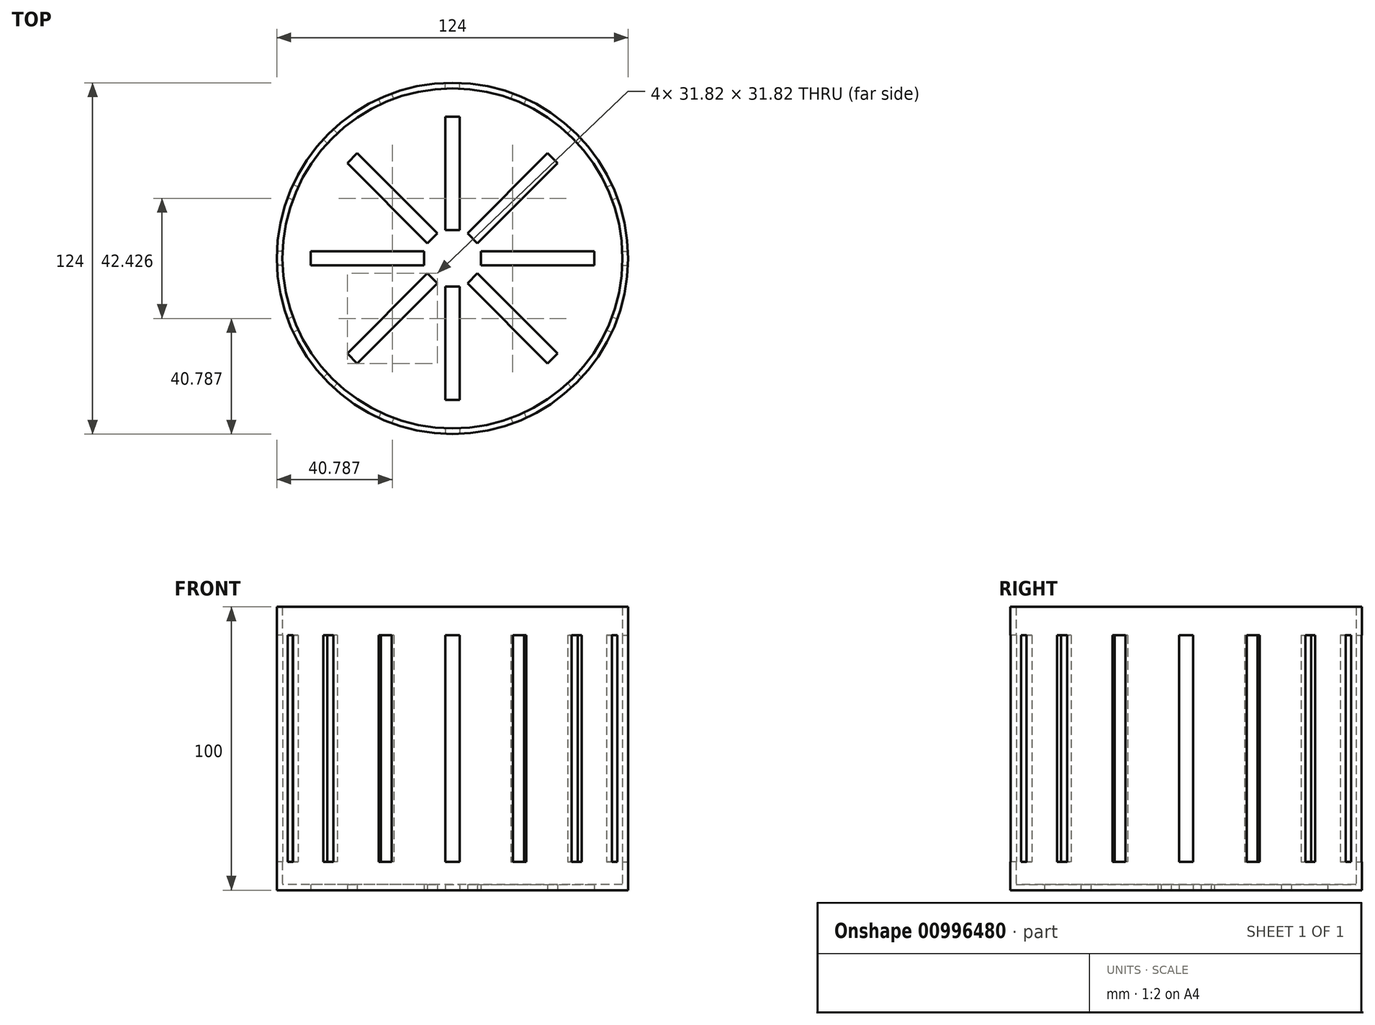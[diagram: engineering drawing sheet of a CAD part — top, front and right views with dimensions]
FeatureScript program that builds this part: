
annotation { "Feature Type Name" : "Feature", "Feature Type Description" : "" }
export const myFeature = defineFeature(function(context is Context, id is Id, definition is map)
    precondition{}
    {
        {
            var Q0;
            Q0=qCreatedBy(makeId("Top.planeOp"),FACE);
            var sketch = newSketch(context, id + "F0", { "sketchPlane" : qUnion([Q0])});
            skCircle(sketch, "E0", {"center": v(0, 0) * mm, "radius": 60 * mm});
            skLineSegment(sketch, "E1", {"start": v(0, 66.92) * mm, "end": v(0, -68.72) * mm, "construction": true});
            skLineSegment(sketch, "E2.bottom", {"start": v(2.5, 10) * mm, "end": v(-2.5, 10) * mm});
            skLineSegment(sketch, "E2.top", {"start": v(2.5, 50) * mm, "end": v(-2.5, 50) * mm});
            skLineSegment(sketch, "E2.left", {"start": v(2.5, 10) * mm, "end": v(2.5, 50) * mm});
            skLineSegment(sketch, "E2.right", {"start": v(-2.5, 10) * mm, "end": v(-2.5, 50) * mm});
            skPoint(sketch, "E2.middle", {"position": v(0, 30) * mm});
            skPoint(sketch, "E3.1.0", {"position": v(-21.21, 21.21) * mm});
            skLineSegment(sketch, "E3.1.1", {"start": v(-8.84, 5.3) * mm, "end": v(-37.12, 33.59) * mm});
            skLineSegment(sketch, "E3.1.2", {"start": v(-5.3, 8.84) * mm, "end": v(-33.59, 37.12) * mm});
            skLineSegment(sketch, "E3.1.3", {"start": v(-33.59, 37.12) * mm, "end": v(-37.12, 33.59) * mm});
            skLineSegment(sketch, "E3.1.4", {"start": v(-5.3, 8.84) * mm, "end": v(-8.84, 5.3) * mm});
            skPoint(sketch, "E3.2.0", {"position": v(-30, 0) * mm});
            skLineSegment(sketch, "E3.2.1", {"start": v(-10, -2.5) * mm, "end": v(-50, -2.5) * mm});
            skLineSegment(sketch, "E3.2.2", {"start": v(-10, 2.5) * mm, "end": v(-50, 2.5) * mm});
            skLineSegment(sketch, "E3.2.3", {"start": v(-50, 2.5) * mm, "end": v(-50, -2.5) * mm});
            skLineSegment(sketch, "E3.2.4", {"start": v(-10, 2.5) * mm, "end": v(-10, -2.5) * mm});
            skPoint(sketch, "E3.3.0", {"position": v(-21.21, -21.21) * mm});
            skLineSegment(sketch, "E3.3.1", {"start": v(-5.3, -8.84) * mm, "end": v(-33.59, -37.12) * mm});
            skLineSegment(sketch, "E3.3.2", {"start": v(-8.84, -5.3) * mm, "end": v(-37.12, -33.59) * mm});
            skLineSegment(sketch, "E3.3.3", {"start": v(-37.12, -33.59) * mm, "end": v(-33.59, -37.12) * mm});
            skLineSegment(sketch, "E3.3.4", {"start": v(-8.84, -5.3) * mm, "end": v(-5.3, -8.84) * mm});
            skPoint(sketch, "E3.4.0", {"position": v(0, -30) * mm});
            skLineSegment(sketch, "E3.4.1", {"start": v(2.5, -10) * mm, "end": v(2.5, -50) * mm});
            skLineSegment(sketch, "E3.4.2", {"start": v(-2.5, -10) * mm, "end": v(-2.5, -50) * mm});
            skLineSegment(sketch, "E3.4.3", {"start": v(-2.5, -50) * mm, "end": v(2.5, -50) * mm});
            skLineSegment(sketch, "E3.4.4", {"start": v(-2.5, -10) * mm, "end": v(2.5, -10) * mm});
            skPoint(sketch, "E3.5.0", {"position": v(21.21, -21.21) * mm});
            skLineSegment(sketch, "E3.5.1", {"start": v(8.84, -5.3) * mm, "end": v(37.12, -33.59) * mm});
            skLineSegment(sketch, "E3.5.2", {"start": v(5.3, -8.84) * mm, "end": v(33.59, -37.12) * mm});
            skLineSegment(sketch, "E3.5.3", {"start": v(33.59, -37.12) * mm, "end": v(37.12, -33.59) * mm});
            skLineSegment(sketch, "E3.5.4", {"start": v(5.3, -8.84) * mm, "end": v(8.84, -5.3) * mm});
            skPoint(sketch, "E3.6.0", {"position": v(30, 0) * mm});
            skLineSegment(sketch, "E3.6.1", {"start": v(10, 2.5) * mm, "end": v(50, 2.5) * mm});
            skLineSegment(sketch, "E3.6.2", {"start": v(10, -2.5) * mm, "end": v(50, -2.5) * mm});
            skLineSegment(sketch, "E3.6.3", {"start": v(50, -2.5) * mm, "end": v(50, 2.5) * mm});
            skLineSegment(sketch, "E3.6.4", {"start": v(10, -2.5) * mm, "end": v(10, 2.5) * mm});
            skPoint(sketch, "E3.7.0", {"position": v(21.21, 21.21) * mm});
            skLineSegment(sketch, "E3.7.1", {"start": v(5.3, 8.84) * mm, "end": v(33.59, 37.12) * mm});
            skLineSegment(sketch, "E3.7.2", {"start": v(8.84, 5.3) * mm, "end": v(37.12, 33.59) * mm});
            skLineSegment(sketch, "E3.7.3", {"start": v(37.12, 33.59) * mm, "end": v(33.59, 37.12) * mm});
            skLineSegment(sketch, "E3.7.4", {"start": v(8.84, 5.3) * mm, "end": v(5.3, 8.84) * mm});
            skCircle(sketch, "E4", {"center": v(0, 0) * mm, "radius": 62 * mm});
            skLineSegment(sketch, "E5", {"start": v(-2.5, -59.95) * mm, "end": v(-2.5, -61.95) * mm});
            skLineSegment(sketch, "E6", {"start": v(2.5, -59.95) * mm, "end": v(2.5, -61.95) * mm});
            skSolve(sketch);
        }
        {
            var Q0;
            Q0=makeQuery(id+"F0.imprint","IMPRINT",FACE,{"disambiguationData":[TD([[makeQuery(id+"F0.imprint","IMPRINT",EDGE,{"derivedFrom":sQuery(id+"F0.wireOp",EDGE,"E0")}),1.0]])]});
            var Q1;
            Q1=makeQuery(id+"F0.imprint","IMPRINT",FACE,{"disambiguationData":[TD([[makeQuery(id+"F0.imprint","IMPRINT",EDGE,{"derivedFrom":sQuery(id+"F0.wireOp",EDGE,"E0")}),-1.0]])]});
            extrude(context, id + "F1", {"entities" : qUnion([Q0, Q1]), "depth" : 2 * mm, "offsetDistance" : 25 * mm});
        }
        {
            var Q0;
            Q0=makeQuery(id+"F0.imprint","IMPRINT",FACE,{"disambiguationData":[TD([[makeQuery(id+"F0.imprint","IMPRINT",EDGE,{"derivedFrom":sQuery(id+"F0.wireOp",EDGE,"E0")}),-1.0]])]});
            extrude(context, id + "F2", {"entities" : qUnion([Q0]), "operationType" : NewBodyOperationType.ADD, "depth" : 100 * mm, "offsetDistance" : 25 * mm});
        }
        {
            var Q0;
            Q0=qCreatedBy(makeId("Top.planeOp"),FACE);
            cPlane(context, id + "F3", {"entities" : qUnion([Q0]), "cplaneType" : CPlaneType.OFFSET, "offset" : 10 * mm, "width" : 150 * mm, "height" : 150 * mm});
        }
        {
            var Q0;
            Q0=qCreatedBy(id+"F3.planeOp",FACE);
            var sketch = newSketch(context, id + "F4", { "sketchPlane" : qUnion([Q0])});
            skLineSegment(sketch, "E7", {"start": v(-2.5, -59.95) * mm, "end": v(-2.5, -61.95) * mm});
            skLineSegment(sketch, "E8", {"start": v(2.5, -59.95) * mm, "end": v(2.5, -61.95) * mm});
            skArc(sketch, "E9", {"start": v(-2.5, -61.95) * mm, "mid": v(0, -62.08) * mm, "end": v(2.5, -61.95) * mm});
            skArc(sketch, "E10", {"start": v(-2.5, -59.95) * mm, "mid": v(0, -59.8) * mm, "end": v(2.5, -59.95) * mm});
            skArc(sketch, "E11.1.0", {"start": v(21.4, -58.2) * mm, "mid": v(23.76, -57.35) * mm, "end": v(26.02, -56.28) * mm});
            skArc(sketch, "E11.1.1", {"start": v(20.63, -56.34) * mm, "mid": v(22.89, -55.25) * mm, "end": v(25.25, -54.43) * mm});
            skLineSegment(sketch, "E11.1.2", {"start": v(20.63, -56.34) * mm, "end": v(21.4, -58.2) * mm});
            skLineSegment(sketch, "E11.1.3", {"start": v(25.25, -54.43) * mm, "end": v(26.02, -56.28) * mm});
            skArc(sketch, "E11.2.0", {"start": v(42.04, -45.57) * mm, "mid": v(43.9, -43.9) * mm, "end": v(45.57, -42.04) * mm});
            skArc(sketch, "E11.2.1", {"start": v(40.62, -44.16) * mm, "mid": v(42.29, -42.29) * mm, "end": v(44.16, -40.62) * mm});
            skLineSegment(sketch, "E11.2.2", {"start": v(40.62, -44.16) * mm, "end": v(42.04, -45.57) * mm});
            skLineSegment(sketch, "E11.2.3", {"start": v(44.16, -40.62) * mm, "end": v(45.57, -42.04) * mm});
            skArc(sketch, "E11.3.0", {"start": v(56.28, -26.02) * mm, "mid": v(57.35, -23.76) * mm, "end": v(58.2, -21.4) * mm});
            skArc(sketch, "E11.3.1", {"start": v(54.43, -25.25) * mm, "mid": v(55.25, -22.89) * mm, "end": v(56.34, -20.63) * mm});
            skLineSegment(sketch, "E11.3.2", {"start": v(54.43, -25.25) * mm, "end": v(56.28, -26.02) * mm});
            skLineSegment(sketch, "E11.3.3", {"start": v(56.34, -20.63) * mm, "end": v(58.2, -21.4) * mm});
            skArc(sketch, "E11.4.0", {"start": v(61.95, -2.5) * mm, "mid": v(62.08, 0) * mm, "end": v(61.95, 2.5) * mm});
            skArc(sketch, "E11.4.1", {"start": v(59.95, -2.5) * mm, "mid": v(59.8, 0) * mm, "end": v(59.95, 2.5) * mm});
            skLineSegment(sketch, "E11.4.2", {"start": v(59.95, -2.5) * mm, "end": v(61.95, -2.5) * mm});
            skLineSegment(sketch, "E11.4.3", {"start": v(59.95, 2.5) * mm, "end": v(61.95, 2.5) * mm});
            skArc(sketch, "E11.5.0", {"start": v(58.2, 21.4) * mm, "mid": v(57.35, 23.76) * mm, "end": v(56.28, 26.02) * mm});
            skArc(sketch, "E11.5.1", {"start": v(56.34, 20.63) * mm, "mid": v(55.25, 22.89) * mm, "end": v(54.43, 25.25) * mm});
            skLineSegment(sketch, "E11.5.2", {"start": v(56.34, 20.63) * mm, "end": v(58.2, 21.4) * mm});
            skLineSegment(sketch, "E11.5.3", {"start": v(54.43, 25.25) * mm, "end": v(56.28, 26.02) * mm});
            skArc(sketch, "E11.6.0", {"start": v(45.57, 42.04) * mm, "mid": v(43.9, 43.9) * mm, "end": v(42.04, 45.57) * mm});
            skArc(sketch, "E11.6.1", {"start": v(44.16, 40.62) * mm, "mid": v(42.29, 42.29) * mm, "end": v(40.62, 44.16) * mm});
            skLineSegment(sketch, "E11.6.2", {"start": v(44.16, 40.62) * mm, "end": v(45.57, 42.04) * mm});
            skLineSegment(sketch, "E11.6.3", {"start": v(40.62, 44.16) * mm, "end": v(42.04, 45.57) * mm});
            skArc(sketch, "E11.7.0", {"start": v(26.02, 56.28) * mm, "mid": v(23.76, 57.35) * mm, "end": v(21.4, 58.2) * mm});
            skArc(sketch, "E11.7.1", {"start": v(25.25, 54.43) * mm, "mid": v(22.89, 55.25) * mm, "end": v(20.63, 56.34) * mm});
            skLineSegment(sketch, "E11.7.2", {"start": v(25.25, 54.43) * mm, "end": v(26.02, 56.28) * mm});
            skLineSegment(sketch, "E11.7.3", {"start": v(20.63, 56.34) * mm, "end": v(21.4, 58.2) * mm});
            skArc(sketch, "E11.8.0", {"start": v(2.5, 61.95) * mm, "mid": v(0, 62.08) * mm, "end": v(-2.5, 61.95) * mm});
            skArc(sketch, "E11.8.1", {"start": v(2.5, 59.95) * mm, "mid": v(0, 59.8) * mm, "end": v(-2.5, 59.95) * mm});
            skLineSegment(sketch, "E11.8.2", {"start": v(2.5, 59.95) * mm, "end": v(2.5, 61.95) * mm});
            skLineSegment(sketch, "E11.8.3", {"start": v(-2.5, 59.95) * mm, "end": v(-2.5, 61.95) * mm});
            skArc(sketch, "E11.9.0", {"start": v(-21.4, 58.2) * mm, "mid": v(-23.76, 57.35) * mm, "end": v(-26.02, 56.28) * mm});
            skArc(sketch, "E11.9.1", {"start": v(-20.63, 56.34) * mm, "mid": v(-22.89, 55.25) * mm, "end": v(-25.25, 54.43) * mm});
            skLineSegment(sketch, "E11.9.2", {"start": v(-20.63, 56.34) * mm, "end": v(-21.4, 58.2) * mm});
            skLineSegment(sketch, "E11.9.3", {"start": v(-25.25, 54.43) * mm, "end": v(-26.02, 56.28) * mm});
            skArc(sketch, "E11.10.0", {"start": v(-42.04, 45.57) * mm, "mid": v(-43.9, 43.9) * mm, "end": v(-45.57, 42.04) * mm});
            skArc(sketch, "E11.10.1", {"start": v(-40.62, 44.16) * mm, "mid": v(-42.29, 42.29) * mm, "end": v(-44.16, 40.62) * mm});
            skLineSegment(sketch, "E11.10.2", {"start": v(-40.62, 44.16) * mm, "end": v(-42.04, 45.57) * mm});
            skLineSegment(sketch, "E11.10.3", {"start": v(-44.16, 40.62) * mm, "end": v(-45.57, 42.04) * mm});
            skArc(sketch, "E11.11.0", {"start": v(-56.28, 26.02) * mm, "mid": v(-57.35, 23.76) * mm, "end": v(-58.2, 21.4) * mm});
            skArc(sketch, "E11.11.1", {"start": v(-54.43, 25.25) * mm, "mid": v(-55.25, 22.89) * mm, "end": v(-56.34, 20.63) * mm});
            skLineSegment(sketch, "E11.11.2", {"start": v(-54.43, 25.25) * mm, "end": v(-56.28, 26.02) * mm});
            skLineSegment(sketch, "E11.11.3", {"start": v(-56.34, 20.63) * mm, "end": v(-58.2, 21.4) * mm});
            skArc(sketch, "E11.12.0", {"start": v(-61.95, 2.5) * mm, "mid": v(-62.08, 0) * mm, "end": v(-61.95, -2.5) * mm});
            skArc(sketch, "E11.12.1", {"start": v(-59.95, 2.5) * mm, "mid": v(-59.8, 0) * mm, "end": v(-59.95, -2.5) * mm});
            skLineSegment(sketch, "E11.12.2", {"start": v(-59.95, 2.5) * mm, "end": v(-61.95, 2.5) * mm});
            skLineSegment(sketch, "E11.12.3", {"start": v(-59.95, -2.5) * mm, "end": v(-61.95, -2.5) * mm});
            skArc(sketch, "E11.13.0", {"start": v(-58.2, -21.4) * mm, "mid": v(-57.35, -23.76) * mm, "end": v(-56.28, -26.02) * mm});
            skArc(sketch, "E11.13.1", {"start": v(-56.34, -20.63) * mm, "mid": v(-55.25, -22.89) * mm, "end": v(-54.43, -25.25) * mm});
            skLineSegment(sketch, "E11.13.2", {"start": v(-56.34, -20.63) * mm, "end": v(-58.2, -21.4) * mm});
            skLineSegment(sketch, "E11.13.3", {"start": v(-54.43, -25.25) * mm, "end": v(-56.28, -26.02) * mm});
            skArc(sketch, "E11.14.0", {"start": v(-45.57, -42.04) * mm, "mid": v(-43.9, -43.9) * mm, "end": v(-42.04, -45.57) * mm});
            skArc(sketch, "E11.14.1", {"start": v(-44.16, -40.62) * mm, "mid": v(-42.29, -42.29) * mm, "end": v(-40.62, -44.16) * mm});
            skLineSegment(sketch, "E11.14.2", {"start": v(-44.16, -40.62) * mm, "end": v(-45.57, -42.04) * mm});
            skLineSegment(sketch, "E11.14.3", {"start": v(-40.62, -44.16) * mm, "end": v(-42.04, -45.57) * mm});
            skArc(sketch, "E11.15.0", {"start": v(-26.02, -56.28) * mm, "mid": v(-23.76, -57.35) * mm, "end": v(-21.4, -58.2) * mm});
            skArc(sketch, "E11.15.1", {"start": v(-25.25, -54.43) * mm, "mid": v(-22.89, -55.25) * mm, "end": v(-20.63, -56.34) * mm});
            skLineSegment(sketch, "E11.15.2", {"start": v(-25.25, -54.43) * mm, "end": v(-26.02, -56.28) * mm});
            skLineSegment(sketch, "E11.15.3", {"start": v(-20.63, -56.34) * mm, "end": v(-21.4, -58.2) * mm});
            skPoint(sketch, "E11.center", {"position": v(0, 0) * mm});
            skSolve(sketch);
        }
        {
            var Q0;
            Q0=makeQuery(id+"F4.imprint","IMPRINT",FACE,{"disambiguationData":[TD([[makeQuery(id+"F4.imprint","IMPRINT",EDGE,{"derivedFrom":sQuery(id+"F4.wireOp",EDGE,"E7")}),1.0]])]});
            var Q1;
            Q1=makeQuery(id+"F4.imprint","IMPRINT",FACE,{"disambiguationData":[TD([[makeQuery(id+"F4.imprint","IMPRINT",EDGE,{"derivedFrom":sQuery(id+"F4.wireOp",EDGE,"E11.15.0")}),1.0]])]});
            var Q2;
            Q2=makeQuery(id+"F4.imprint","IMPRINT",FACE,{"disambiguationData":[TD([[makeQuery(id+"F4.imprint","IMPRINT",EDGE,{"derivedFrom":sQuery(id+"F4.wireOp",EDGE,"E11.14.0")}),1.0]])]});
            var Q3;
            Q3=makeQuery(id+"F4.imprint","IMPRINT",FACE,{"disambiguationData":[TD([[makeQuery(id+"F4.imprint","IMPRINT",EDGE,{"derivedFrom":sQuery(id+"F4.wireOp",EDGE,"E11.13.0")}),1.0]])]});
            var Q4;
            Q4=makeQuery(id+"F4.imprint","IMPRINT",FACE,{"disambiguationData":[TD([[makeQuery(id+"F4.imprint","IMPRINT",EDGE,{"derivedFrom":sQuery(id+"F4.wireOp",EDGE,"E11.12.0")}),1.0]])]});
            var Q5;
            Q5=makeQuery(id+"F4.imprint","IMPRINT",FACE,{"disambiguationData":[TD([[makeQuery(id+"F4.imprint","IMPRINT",EDGE,{"derivedFrom":sQuery(id+"F4.wireOp",EDGE,"E11.1.0")}),1.0]])]});
            var Q6;
            Q6=makeQuery(id+"F4.imprint","IMPRINT",FACE,{"disambiguationData":[TD([[makeQuery(id+"F4.imprint","IMPRINT",EDGE,{"derivedFrom":sQuery(id+"F4.wireOp",EDGE,"E11.2.0")}),1.0]])]});
            var Q7;
            Q7=makeQuery(id+"F4.imprint","IMPRINT",FACE,{"disambiguationData":[TD([[makeQuery(id+"F4.imprint","IMPRINT",EDGE,{"derivedFrom":sQuery(id+"F4.wireOp",EDGE,"E11.3.0")}),1.0]])]});
            var Q8;
            Q8=makeQuery(id+"F4.imprint","IMPRINT",FACE,{"disambiguationData":[TD([[makeQuery(id+"F4.imprint","IMPRINT",EDGE,{"derivedFrom":sQuery(id+"F4.wireOp",EDGE,"E11.5.0")}),1.0]])]});
            var Q9;
            Q9=makeQuery(id+"F4.imprint","IMPRINT",FACE,{"disambiguationData":[TD([[makeQuery(id+"F4.imprint","IMPRINT",EDGE,{"derivedFrom":sQuery(id+"F4.wireOp",EDGE,"E11.6.0")}),1.0]])]});
            var Q10;
            Q10=makeQuery(id+"F4.imprint","IMPRINT",FACE,{"disambiguationData":[TD([[makeQuery(id+"F4.imprint","IMPRINT",EDGE,{"derivedFrom":sQuery(id+"F4.wireOp",EDGE,"E11.7.0")}),1.0]])]});
            var Q11;
            Q11=makeQuery(id+"F4.imprint","IMPRINT",FACE,{"disambiguationData":[TD([[makeQuery(id+"F4.imprint","IMPRINT",EDGE,{"derivedFrom":sQuery(id+"F4.wireOp",EDGE,"E11.8.0")}),1.0]])]});
            var Q12;
            Q12=makeQuery(id+"F4.imprint","IMPRINT",FACE,{"disambiguationData":[TD([[makeQuery(id+"F4.imprint","IMPRINT",EDGE,{"derivedFrom":sQuery(id+"F4.wireOp",EDGE,"E11.9.0")}),1.0]])]});
            var Q13;
            Q13=makeQuery(id+"F4.imprint","IMPRINT",FACE,{"disambiguationData":[TD([[makeQuery(id+"F4.imprint","IMPRINT",EDGE,{"derivedFrom":sQuery(id+"F4.wireOp",EDGE,"E11.11.0")}),1.0]])]});
            var Q14;
            Q14=makeQuery(id+"F4.imprint","IMPRINT",FACE,{"disambiguationData":[TD([[makeQuery(id+"F4.imprint","IMPRINT",EDGE,{"derivedFrom":sQuery(id+"F4.wireOp",EDGE,"E11.10.0")}),1.0]])]});
            var Q15;
            Q15=makeQuery(id+"F4.imprint","IMPRINT",FACE,{"disambiguationData":[TD([[makeQuery(id+"F4.imprint","IMPRINT",EDGE,{"derivedFrom":sQuery(id+"F4.wireOp",EDGE,"E11.4.0")}),1.0]])]});
            extrude(context, id + "F5", {"entities" : qUnion([Q0, Q1, Q2, Q3, Q4, Q5, Q6, Q7, Q8, Q9, Q10, Q11, Q12, Q13, Q14, Q15]), "operationType" : NewBodyOperationType.REMOVE, "depth" : 80 * mm, "offsetDistance" : 25 * mm});
        }
    });
